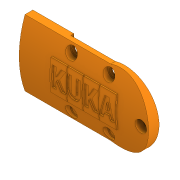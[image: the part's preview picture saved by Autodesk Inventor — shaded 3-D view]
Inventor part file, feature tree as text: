
AUTODESK INVENTOR PART (.ipt)
format: ipt  version: 2020 (Build 240168000, 168)  size: 601,600 bytes
history: native  units: in
note: dims shown in document units (in); Inventor stores cm internally (conversion verified against a paired STEP export)
features: sketch x16, extrude x15, plane x3, projected_geometry x3, fillet x1, emboss x1
ambient origin geometry x8: Origin, YZ Plane, XZ Plane, XY Plane, X Axis, Y Axis, Z Axis, Center Point
bodies: Solid1 (feature_tree)
feature tree (39):
  extrude  "Extrusion1"  Depth=0.2362in
  extrude  "Extrusion2"  Depth=0.2362in
  extrude  "Extrusion3"  Depth=0.2362in
  fillet  "Fillet1"  Radius=0.2264in
  plane  "Work Plane1"
  extrude  "Extrusion4"  Depth=0.1969in
  sketch  "Sketch5"  dims[d11=0.0in d12=0.0in d13=0.0787in]
  extrude  "Extrusion5"  Depth=0.0787in
  extrude  "Extrusion6"  Depth=0.5512in
  extrude  "Extrusion7"  Depth=0.9843in
  emboss  "Emboss1"
  plane  "Work Plane2"
  extrude  "Extrusion8"  Depth=0.0787in
  extrude  "Extrusion9"  Depth=0.0197in
  extrude  "Extrusion10"  Depth=0.0787in TaperAngle=0.0deg
  extrude  "Extrusion11"  Depth=0.0394in TaperAngle=0.0deg
  plane  "Work Plane3"
  extrude  "Extrusion12"  Depth=0.3543in
  extrude  "Extrusion13"  Depth=0.3543in
  extrude  "Extrusion14"  Depth=0.4724in TaperAngle=0.0deg
  extrude  "Extrusion15"  Depth=0.5512in
  sketch  "Sketch1"  dims[d0=0.1575in d1=0.2362in]
  sketch  "Sketch2"  dims[d2=0.2362in d3=0.2362in]
  sketch  "Sketch3"  dims[d4=0.2362in d5=0.2362in d6=0.2264in d7=0.0in]
  sketch  "Sketch4"  dims[d8=0.1969in d9=0.0in d10=0.1969in]
  projected_geometry  "Projected Loop1"
  sketch  "Sketch6"  dims[d14=0.5512in d15=0.5512in]
  sketch  "Sketch7"  dims[d16=0.9843in d17=0.9843in]
  sketch  "Sketch8"  dims[d18=0.0787in d19=0.0in d20=0.0197in]
  sketch  "Sketch9"  dims[d21=0.0197in d22=0.0197in]
  sketch  "Sketch10"  dims[d23=0.0in d24=0.0in d25=0.0787in d26=0.0in]
  sketch  "Sketch11"  dims[d27=0.0in d28=0.0in d29=0.0394in d30=0.0in]
  sketch  "Sketch12"  dims[d31=0.3543in d32=0.3543in]
  sketch  "Sketch13"  dims[d33=0.3543in d34=0.3543in]
  projected_geometry  "Projected Loop2"
  sketch  "Sketch14"  dims[d35=0.3543in d36=0.4724in d37=0.0in]
  projected_geometry  "Projected Loop3"
  sketch  "Sketch15"  dims[d38=0.315in d39=0.5512in]
  sketch  "Sketch16"  dims[d40=0.0984in d41=0.0in d42=0.0984in d43=0.0in d44=0.2362in d45=0.0394in d46=0.0in d47=0.0in d49=0.0079in d50=0.0988in d51=0.0in d52=0.0988in d53=0.0in d54=0.5787in d55=0.0433in d56=0.0in d57=0.2756in d58=0.0787in d59=0.0in]
